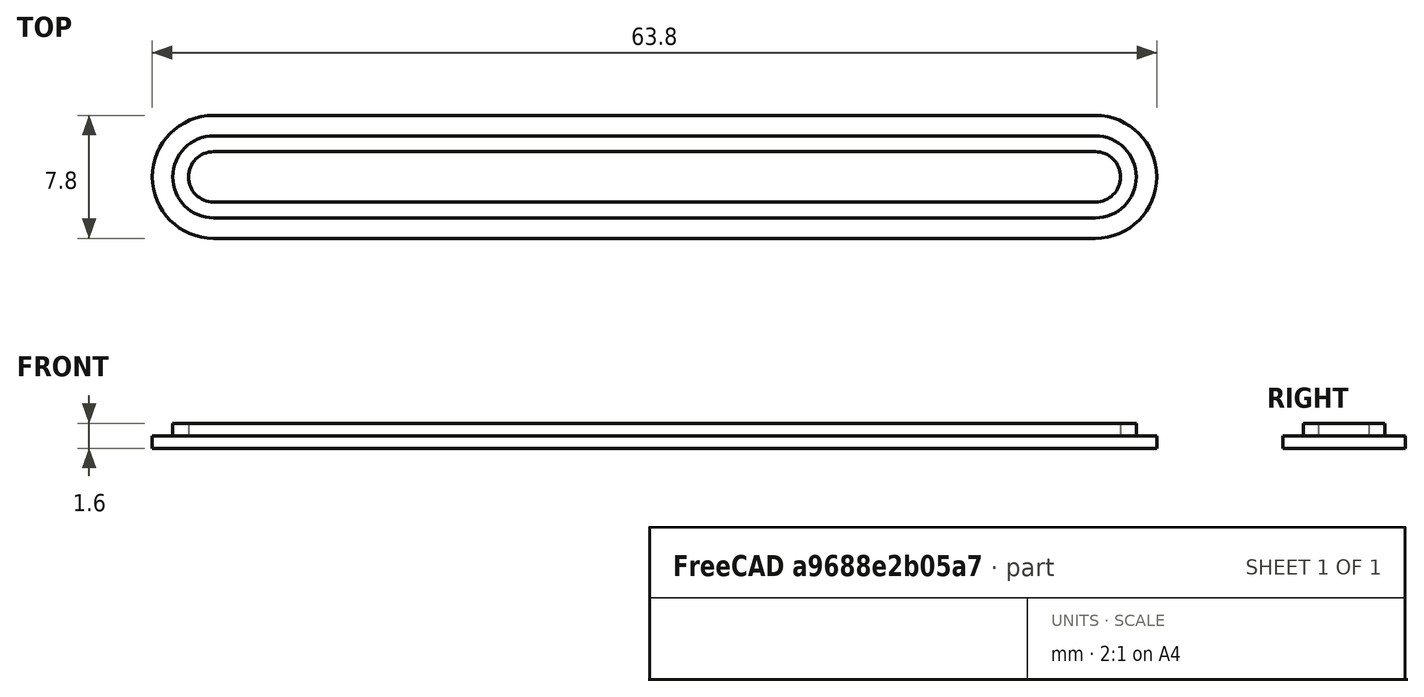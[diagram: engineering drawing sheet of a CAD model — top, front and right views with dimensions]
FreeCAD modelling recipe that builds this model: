
FCSTD DOCUMENT  (FreeCAD 1.0R38641 +678 (Git))
Label: CyberInset2
License: All rights reserved
LicenseURL: https://en.wikipedia.org/wiki/All_rights_reserved
objects: Sketcher::SketchObject×2, PartDesign::Pad×2, PartDesign::Body×1, Mesh::Feature×1
note: 11 computed .brp shape members not serialized (recipe doc carries the construction recipe); baked Part::Feature solids carry a one-line shape summary decoded from their .brp

FEATURE [Sketcher::SketchObject] Sketch
  ArcFitTolerance = 1e-06
  AttachmentSupport = -> [XY_Plane]
  FullyConstrained = true
  MakeInternals = false
  MapMode = 5
  sketch-geometry (4):
    g0: ArcOfCircle CenterX=0 CenterY=0 CenterZ=0 NormalX=0 NormalY=0 NormalZ=1 AngleXU=0 Radius=3.9 StartAngle=1.5708 EndAngle=4.71239
    g1: ArcOfCircle CenterX=56 CenterY=-4.1506e-12 CenterZ=0 NormalX=0 NormalY=0 NormalZ=1 AngleXU=0 Radius=3.9 StartAngle=4.71239 EndAngle=7.85398
    g2: LineSegment StartX=2.842e-13 StartY=3.9 StartZ=0 EndX=56 EndY=3.9 EndZ=0
    g3: LineSegment StartX=-1.67279e-11 StartY=-3.9 StartZ=0 EndX=56 EndY=-3.9 EndZ=0
  constraints (9):
    c: Tangent(g0,g2) = 1.5708
    c: Tangent(g0,g3) = -1.5708
    c: Tangent(g1,g2) = 1.5708
    c: Tangent(g1,g3) = -1.5708
    c: Equal(g0,g1)
    c: Horizontal(g3)
    c: DistanceX(g2,g2) = 56
    c: Radius(g0) = 3.9
    c: Coincident(g0,g-1)
FEATURE [PartDesign::Pad] Pad
  Direction = (0,0,1)
  Length = 0.8
  Length2 = 10
  Profile = -> Sketch
  ReferenceAxis = -> Sketch [N_Axis]
  Refine = true
  Reversed = true
  Suppressed = false
  Type = 0
FEATURE [Sketcher::SketchObject] Sketch001
  ArcFitTolerance = 1e-06
  AttachmentSupport = -> [Pad]
  FullyConstrained = true
  MakeInternals = false
  MapMode = 5
  sketch-geometry (8):
    g0: ArcOfCircle CenterX=0 CenterY=0 CenterZ=0 NormalX=0 NormalY=0 NormalZ=1 AngleXU=0 Radius=2.6 StartAngle=1.5708 EndAngle=4.71239
    g1: ArcOfCircle CenterX=56 CenterY=2e-16 CenterZ=0 NormalX=0 NormalY=0 NormalZ=1 AngleXU=0 Radius=2.6 StartAngle=4.71239 EndAngle=7.85398
    g2: LineSegment StartX=-4e-16 StartY=2.6 StartZ=0 EndX=56 EndY=2.6 EndZ=0
    g3: LineSegment StartX=-5e-16 StartY=-2.6 StartZ=0 EndX=56 EndY=-2.6 EndZ=0
    g4: ArcOfCircle CenterX=0 CenterY=0 CenterZ=0 NormalX=0 NormalY=0 NormalZ=1 AngleXU=0 Radius=1.6 StartAngle=1.5708 EndAngle=4.71239
    g5: ArcOfCircle CenterX=56 CenterY=2e-16 CenterZ=0 NormalX=0 NormalY=0 NormalZ=1 AngleXU=0 Radius=1.6 StartAngle=4.71239 EndAngle=7.85398
    g6: LineSegment StartX=-3e-16 StartY=1.6 StartZ=0 EndX=56 EndY=1.6 EndZ=0
    g7: LineSegment StartX=0 StartY=-1.6 StartZ=0 EndX=56 EndY=-1.6 EndZ=0
  constraints (17):
    c: Tangent(g0,g2) = 1.5708
    c: Tangent(g0,g3) = -1.5708
    c: Tangent(g1,g2) = 1.5708
    c: Tangent(g1,g3) = -1.5708
    c: Equal(g0,g1)
    c: Horizontal(g3)
    c: Coincident(g0,g-1)
    c: DistanceX(g0,g1) = 56
    c: Tangent(g4,g6) = 1.5708
    c: Tangent(g4,g7) = -1.5708
    c: Tangent(g5,g6) = 1.5708
    c: Tangent(g5,g7) = -1.5708
    c: Equal(g4,g5)
    c: Coincident(g4,g0)
    c: Coincident(g5,g1)
    c: Radius(g1) = 2.6
    c: Radius(g5) = 1.6
FEATURE [PartDesign::Pad] Pad001  label="CyberInset"
  BaseFeature = -> Pad
  Direction = (0,0,1)
  Length = 0.8
  Length2 = 10
  Profile = -> Sketch001
  ReferenceAxis = -> Sketch001 [N_Axis]
  Refine = true
  Suppressed = false
  Type = 0
FEATURE [PartDesign::Body] Body
  AllowCompound = false
  Group = -> [Sketch,Pad,Sketch001,Pad001]
  Origin = -> Origin
  Tip = -> Pad001
FEATURE [Mesh::Feature] Mesh  label="CyberInset (Meshed)"
